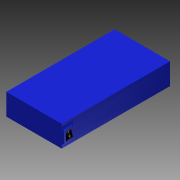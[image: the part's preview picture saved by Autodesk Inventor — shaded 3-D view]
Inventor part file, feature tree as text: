
AUTODESK INVENTOR PART (.ipt)
format: ipt  version: 2014 (Build 180170000, 170)  size: 208,384 bytes
history: native  units: in
note: dims shown in document units (in); Inventor stores cm internally (conversion verified against a paired STEP export)
features: sketch x6, extrude x5, plane x2, projected_geometry x2, fillet x1, emboss x1
ambient origin geometry x8: Origin, YZ Plane, XZ Plane, XY Plane, X Axis, Y Axis, Z Axis, Center Point
bodies: Solid1 (feature_tree)
feature tree (17):
  extrude  "Extrusion1"  Depth=2.59in
  extrude  "Extrusion2"  Depth=0.13in
  extrude  "Extrusion3"  Depth=0.435in
  fillet  "Fillet1"  Radius=0.03in
  extrude  "Extrusion4"  Depth=0.56in
  plane  "Work Plane1"
  extrude  "Extrusion5"  Depth=0.22in
  plane  "Work Plane2"
  emboss  "Emboss1"
  sketch  "Sketch1"  dims[d0=5.06in d1=2.59in]
  sketch  "Sketch2"  dims[d2=1.0in d3=0.0in d4=0.13in]
  sketch  "Sketch3"  dims[d5=0.435in d6=0.435in d7=0.03in]
  sketch  "Sketch4"  dims[d8=0.03in d9=0.0in d10=0.56in]
  projected_geometry  "Projected Loop1"
  sketch  "Sketch5"  dims[d11=0.41in d12=0.22in]
  sketch  "Sketch6"  dims[d13=0.22in d14=0.1in d15=0.0in d16=0.125in d17=0.05in d18=0.105in d19=0.0in d20=-0.1in d21=0.38in d22=0.3in d23=0.07in d24=0.25in d25=0.0in d26=0.03in d27=0.03in d28=0.087in d29=0.04in d30=0.0815in d31=0.0815in d33=0.003in d34=0.0in]
  projected_geometry  "Projected Loop2"
